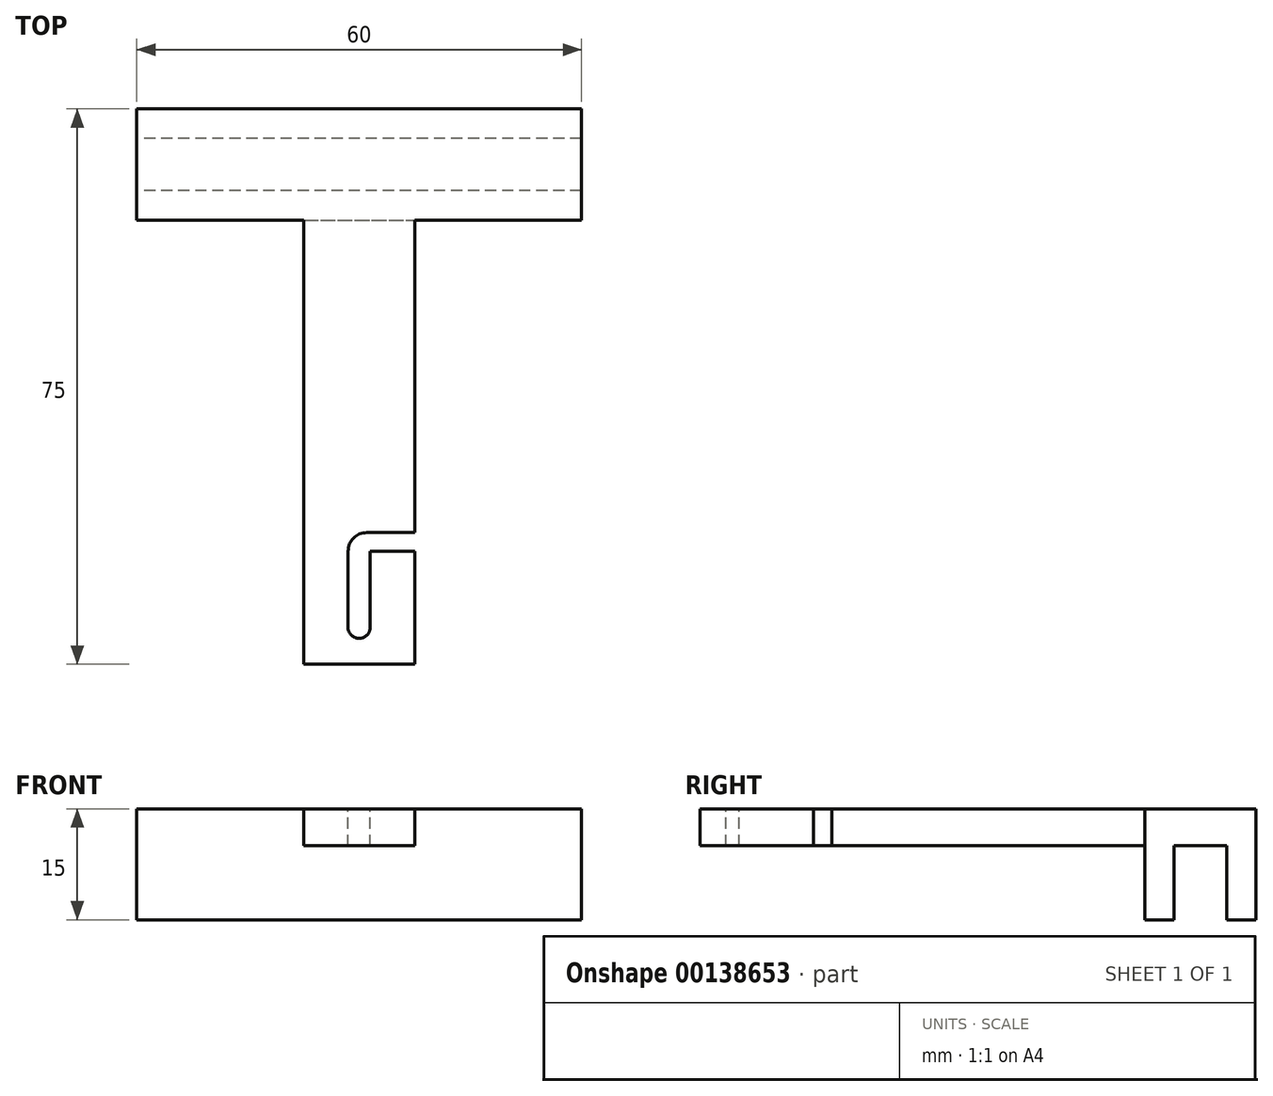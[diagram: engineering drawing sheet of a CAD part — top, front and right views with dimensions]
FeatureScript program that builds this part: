
annotation { "Feature Type Name" : "Feature", "Feature Type Description" : "" }
export const myFeature = defineFeature(function(context is Context, id is Id, definition is map)
    precondition{}
    {
        {
            var Q0;
            Q0=qCreatedBy(makeId("Top.planeOp"),FACE);
            var sketch = newSketch(context, id + "F0", { "sketchPlane" : qUnion([Q0])});
            skLineSegment(sketch, "E0.bottom", {"start": v(-7.5, 30) * mm, "end": v(7.5, 30) * mm});
            skLineSegment(sketch, "E0.top", {"start": v(-7.5, -30) * mm, "end": v(7.5, -30) * mm});
            skLineSegment(sketch, "E0.left", {"start": v(-7.5, 30) * mm, "end": v(-7.5, -30) * mm});
            skLineSegment(sketch, "E0.right", {"start": v(7.5, 30) * mm, "end": v(7.5, -30) * mm});
            skPoint(sketch, "E0.middle", {"position": v(0, 0) * mm});
            skSolve(sketch);
        }
        {
            var Q0;
            Q0=makeQuery(id+"F0.imprint","IMPRINT",FACE,{"disambiguationData":[TD([[makeQuery(id+"F0.imprint","IMPRINT",EDGE,{"derivedFrom":sQuery(id+"F0.wireOp",EDGE,"E0.bottom")}),-1.0]])]});
            extrude(context, id + "F1", {"entities" : qUnion([Q0]), "depth" : 5 * mm});
        }
        {
            var Q0;
            Q0=qCreatedBy(makeId("Top.planeOp"),FACE);
            var sketch = newSketch(context, id + "F2", { "sketchPlane" : qUnion([Q0])});
            skLineSegment(sketch, "E1.bottom", {"start": v(-30, 45) * mm, "end": v(30, 45) * mm});
            skLineSegment(sketch, "E1.top", {"start": v(-30, 30) * mm, "end": v(30, 30) * mm});
            skLineSegment(sketch, "E1.left", {"start": v(-30, 45) * mm, "end": v(-30, 30) * mm});
            skLineSegment(sketch, "E1.right", {"start": v(30, 45) * mm, "end": v(30, 30) * mm});
            skSolve(sketch);
        }
        {
            var Q0;
            Q0=makeQuery(id+"F2.imprint","IMPRINT",FACE,{"disambiguationData":[TD([[makeQuery(id+"F2.imprint","IMPRINT",EDGE,{"derivedFrom":sQuery(id+"F2.wireOp",EDGE,"E1.bottom")}),-1.0]])]});
            extrude(context, id + "F3", {"entities" : qUnion([Q0]), "operationType" : NewBodyOperationType.ADD, "depth" : 5 * mm});
        }
        {
            var Q0;
            Q0=makeQuery(id+"F3.boolean.opBoolean","MERGE",FACE,{"derivedFrom":[makeQuery(id+"F1.opExtrude","CAP_FACE",FACE,{"disambiguationData":[OSD([sQuery(id+"F0.wireOp",EDGE,"E0.bottom"),sQuery(id+"F0.wireOp",EDGE,"E0.top"),sQuery(id+"F0.wireOp",EDGE,"E0.left"),sQuery(id+"F0.wireOp",EDGE,"E0.right")])],"isStart":true}),makeQuery(id+"F3.opExtrude","CAP_FACE",FACE,{"disambiguationData":[OSD([sQuery(id+"F2.wireOp",EDGE,"E1.bottom"),sQuery(id+"F2.wireOp",EDGE,"E1.top"),sQuery(id+"F2.wireOp",EDGE,"E1.left"),sQuery(id+"F2.wireOp",EDGE,"E1.right")])],"isStart":true})]});
            var sketch = newSketch(context, id + "F4", { "sketchPlane" : qUnion([Q0])});
            skLineSegment(sketch, "E2.bottom", {"start": v(30, -45) * mm, "end": v(-30, -45) * mm});
            skLineSegment(sketch, "E2.top", {"start": v(30, -41.05) * mm, "end": v(-30, -41.05) * mm});
            skLineSegment(sketch, "E2.left", {"start": v(30, -45) * mm, "end": v(30, -41.05) * mm});
            skLineSegment(sketch, "E2.right", {"start": v(-30, -45) * mm, "end": v(-30, -41.05) * mm});
            skLineSegment(sketch, "E3.bottom", {"start": v(30, -30) * mm, "end": v(-30, -30) * mm});
            skLineSegment(sketch, "E3.top", {"start": v(30, -33.95) * mm, "end": v(-30, -33.95) * mm});
            skLineSegment(sketch, "E3.left", {"start": v(30, -30) * mm, "end": v(30, -33.95) * mm});
            skLineSegment(sketch, "E3.right", {"start": v(-30, -30) * mm, "end": v(-30, -33.95) * mm});
            skSolve(sketch);
        }
        {
            var Q0;
            Q0 = qSketchRegion(id + "F4", true);
            extrude(context, id + "F5", {"entities" : qUnion([Q0]), "operationType" : NewBodyOperationType.ADD, "depth" : 10 * mm});
        }
        {
            var Q0;
            Q0=makeQuery(id+"F3.boolean.opBoolean","MERGE",FACE,{"derivedFrom":[makeQuery(id+"F1.opExtrude","CAP_FACE",FACE,{"disambiguationData":[OSD([sQuery(id+"F0.wireOp",EDGE,"E0.bottom"),sQuery(id+"F0.wireOp",EDGE,"E0.top"),sQuery(id+"F0.wireOp",EDGE,"E0.left"),sQuery(id+"F0.wireOp",EDGE,"E0.right")])],"isStart":false}),makeQuery(id+"F3.opExtrude","CAP_FACE",FACE,{"disambiguationData":[OSD([sQuery(id+"F2.wireOp",EDGE,"E1.bottom"),sQuery(id+"F2.wireOp",EDGE,"E1.top"),sQuery(id+"F2.wireOp",EDGE,"E1.left"),sQuery(id+"F2.wireOp",EDGE,"E1.right")])],"isStart":false})]});
            var sketch = newSketch(context, id + "F6", { "sketchPlane" : qUnion([Q0])});
            skCircle(sketch, "E4", {"center": v(0, -25) * mm, "radius": 1.5 * mm});
            skSolve(sketch);
        }
        {
            var Q0;
            Q0 = qSketchRegion(id + "F6", true);
            extrude(context, id + "F7", {"entities" : qUnion([Q0]), "operationType" : NewBodyOperationType.REMOVE, "oppositeDirection" : true, "depth" : 25 * mm});
        }
        {
            var Q0;
            Q0=makeQuery(id+"F3.boolean.opBoolean","MERGE",FACE,{"derivedFrom":[makeQuery(id+"F1.opExtrude","CAP_FACE",FACE,{"disambiguationData":[OSD([sQuery(id+"F0.wireOp",EDGE,"E0.bottom"),sQuery(id+"F0.wireOp",EDGE,"E0.top"),sQuery(id+"F0.wireOp",EDGE,"E0.left"),sQuery(id+"F0.wireOp",EDGE,"E0.right")])],"isStart":false}),makeQuery(id+"F3.opExtrude","CAP_FACE",FACE,{"disambiguationData":[OSD([sQuery(id+"F2.wireOp",EDGE,"E1.bottom"),sQuery(id+"F2.wireOp",EDGE,"E1.top"),sQuery(id+"F2.wireOp",EDGE,"E1.left"),sQuery(id+"F2.wireOp",EDGE,"E1.right")])],"isStart":false})]});
            var sketch = newSketch(context, id + "F8", { "sketchPlane" : qUnion([Q0])});
            skLineSegment(sketch, "E5.bottom", {"start": v(-1.48, -24.75) * mm, "end": v(1.5, -24.75) * mm});
            skLineSegment(sketch, "E5.right", {"start": v(1.5, -24.75) * mm, "end": v(1.5, -14.72) * mm});
            skLineSegment(sketch, "E6.bottom", {"start": v(1.5, -14.72) * mm, "end": v(7.5, -14.72) * mm});
            skLineSegment(sketch, "E6.top", {"start": v(-1.48, -12.22) * mm, "end": v(7.5, -12.22) * mm});
            skLineSegment(sketch, "E6.right", {"start": v(7.5, -14.72) * mm, "end": v(7.5, -12.22) * mm});
            skLineSegment(sketch, "E7", {"start": v(-1.48, -12.22) * mm, "end": v(-1.48, -24.75) * mm});
            skSolve(sketch);
        }
        {
            var Q0;
            {var subQ0=sQuery(id+"F8.wireOp",EDGE,"E5.right");Q0=makeQuery(id+"F8.imprint","IMPRINT",FACE,{"disambiguationData":[TD([[makeQuery(id+"F8.imprint","IMPRINT",EDGE,{"derivedFrom":subQ0}),1.0]])]});}
            extrude(context, id + "F9", {"entities" : qUnion([Q0]), "operationType" : NewBodyOperationType.REMOVE, "oppositeDirection" : true, "depth" : 25 * mm});
        }
        {
            var Q0;
            Q0=makeQuery(id+"F9.boolean.opBoolean","COPY",EDGE,{"derivedFrom":makeQuery(id+"F9.opExtrude","SWEPT_EDGE",EDGE,{"disambiguationData":[OSD([sQuery(id+"F8.wireOp",EDGE,"E6.top"),sQuery(id+"F8.wireOp",EDGE,"E7")])]})});
            fillet(context, id + "F10", {"entities" : qUnion([Q0]), "radius" : 2.5 * mm, "tangentPropagation" : true, "allowEdgeOverflow" : false});
        }
    });
